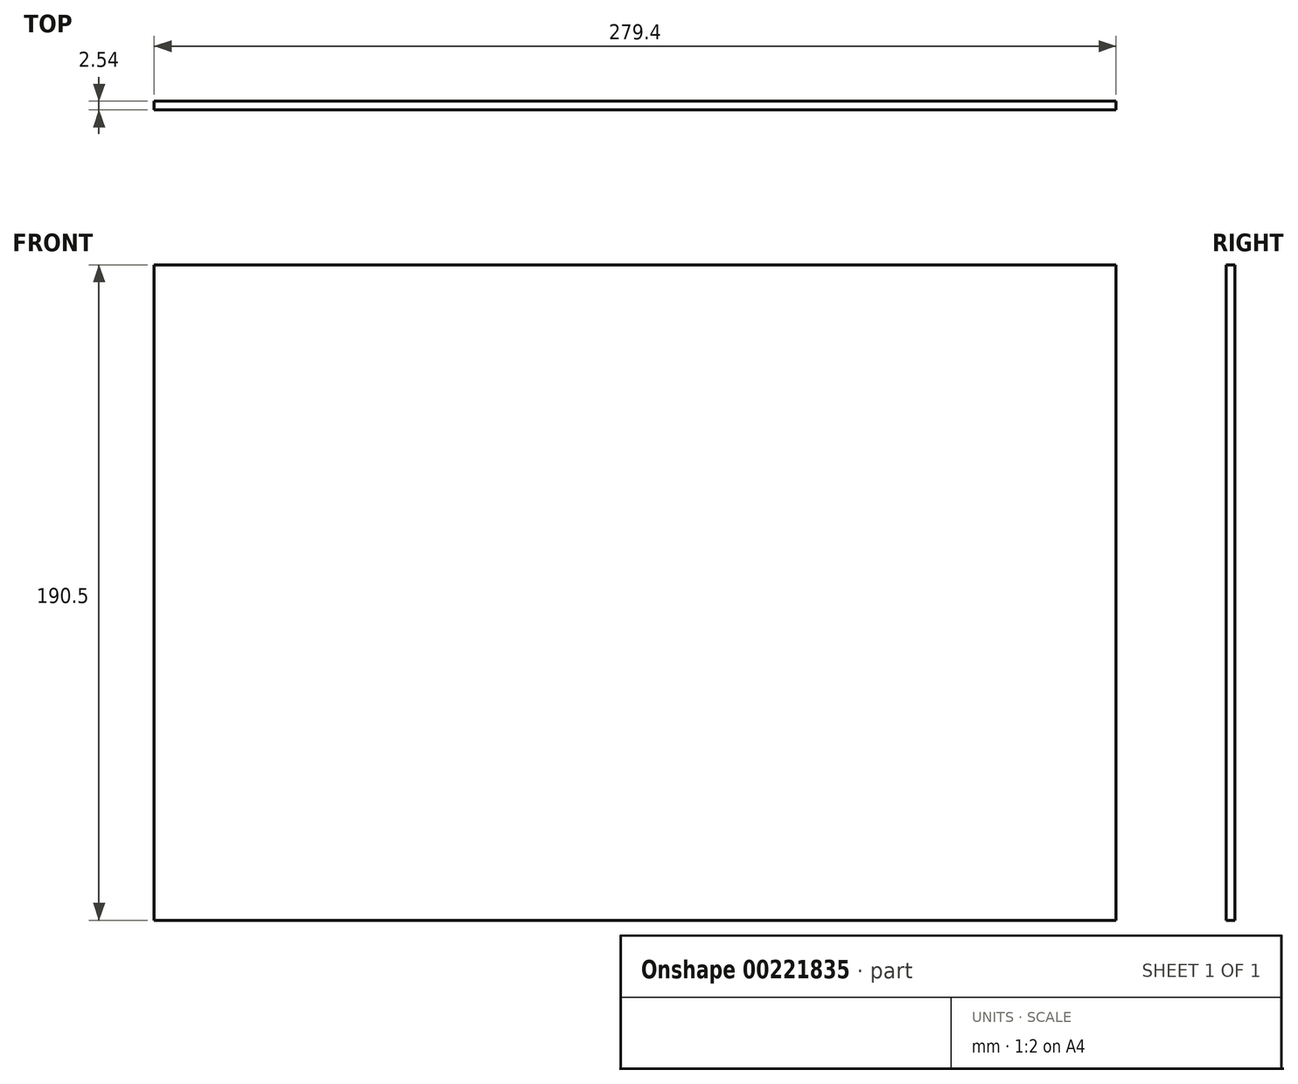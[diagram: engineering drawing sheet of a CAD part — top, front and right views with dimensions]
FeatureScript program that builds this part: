
annotation { "Feature Type Name" : "Feature", "Feature Type Description" : "" }
export const myFeature = defineFeature(function(context is Context, id is Id, definition is map)
    precondition{}
    {
        {
            var Q0;
            Q0=qCreatedBy(makeId("Front.planeOp"),FACE);
            var sketch = newSketch(context, id + "F0", { "sketchPlane" : qUnion([Q0])});
            skLineSegment(sketch, "E0.bottom", {"start": v(139.7, -95.25) * mm, "end": v(-139.7, -95.25) * mm});
            skLineSegment(sketch, "E0.top", {"start": v(139.7, 95.25) * mm, "end": v(-139.7, 95.25) * mm});
            skLineSegment(sketch, "E0.left", {"start": v(139.7, -95.25) * mm, "end": v(139.7, 95.25) * mm});
            skLineSegment(sketch, "E0.right", {"start": v(-139.7, -95.25) * mm, "end": v(-139.7, 95.25) * mm});
            skPoint(sketch, "E0.middle", {"position": v(0, 0) * mm});
            skSolve(sketch);
        }
        {
            var Q0;
            Q0 = qSketchRegion(id + "F0", true);
            extrude(context, id + "F1", {"entities" : qUnion([Q0]), "depth" : 2.54 * mm});
        }
    });
